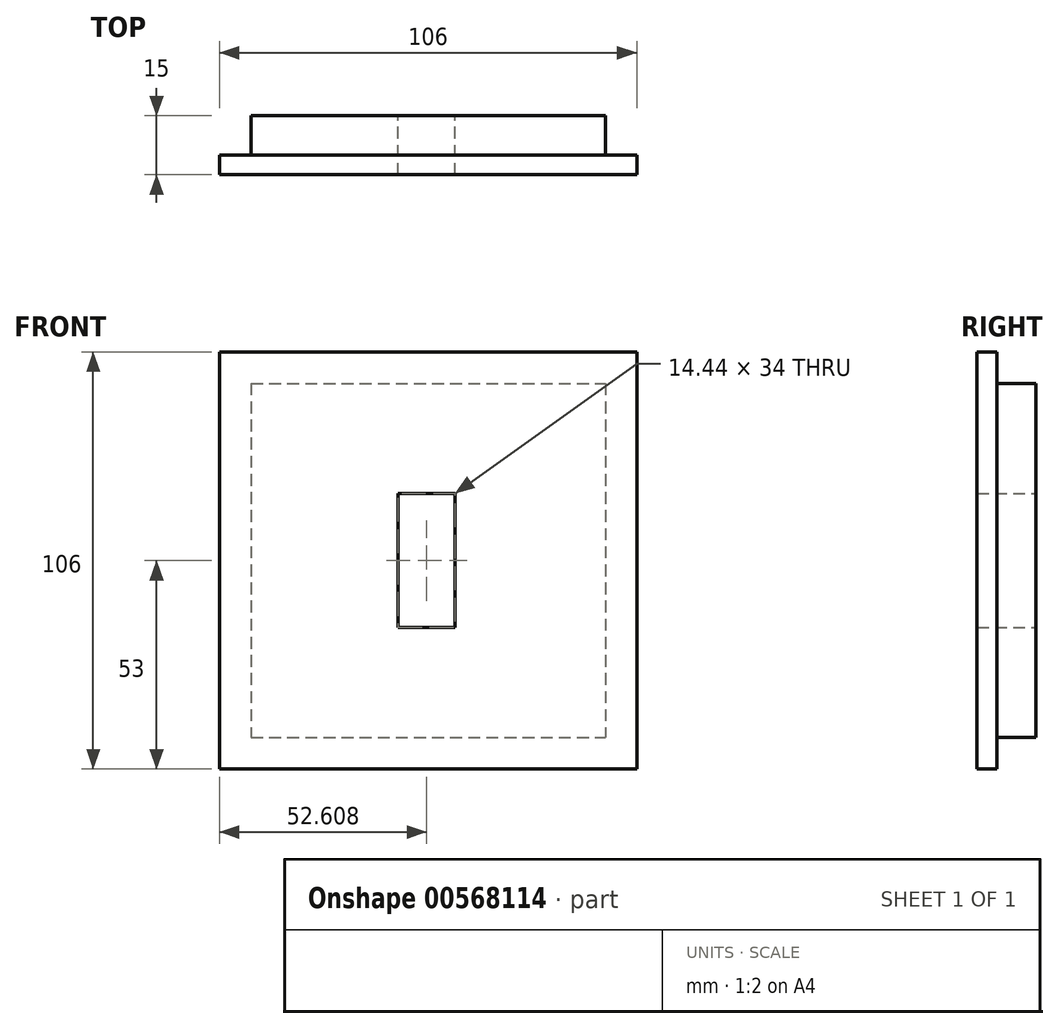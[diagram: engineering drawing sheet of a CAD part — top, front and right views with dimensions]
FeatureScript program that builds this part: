
annotation { "Feature Type Name" : "Feature", "Feature Type Description" : "" }
export const myFeature = defineFeature(function(context is Context, id is Id, definition is map)
    precondition{}
    {
        {
            var Q0;
            Q0=qCreatedBy(makeId("Front.planeOp"),FACE);
            var sketch = newSketch(context, id + "F0", { "sketchPlane" : qUnion([Q0])});
            skLineSegment(sketch, "E0.bottom", {"start": v(-43.54, 60.22) * mm, "end": v(46.46, 60.22) * mm});
            skLineSegment(sketch, "E0.top", {"start": v(-43.54, -29.78) * mm, "end": v(46.46, -29.78) * mm});
            skLineSegment(sketch, "E0.left", {"start": v(-43.54, 60.22) * mm, "end": v(-43.54, -29.78) * mm});
            skLineSegment(sketch, "E0.right", {"start": v(46.46, 60.22) * mm, "end": v(46.46, -29.78) * mm});
            skLineSegment(sketch, "E1.bottom", {"start": v(-51.54, 68.22) * mm, "end": v(54.46, 68.22) * mm});
            skLineSegment(sketch, "E1.top", {"start": v(-51.54, -37.78) * mm, "end": v(54.46, -37.78) * mm});
            skLineSegment(sketch, "E1.left", {"start": v(-51.54, 68.22) * mm, "end": v(-51.54, -37.78) * mm});
            skLineSegment(sketch, "E1.right", {"start": v(54.46, 68.22) * mm, "end": v(54.46, -37.78) * mm});
            skSolve(sketch);
        }
        {
            var Q0;
            Q0=makeQuery(id+"F0.imprint","IMPRINT",FACE,{"disambiguationData":[TD([[makeQuery(id+"F0.imprint","IMPRINT",EDGE,{"derivedFrom":sQuery(id+"F0.wireOp",EDGE,"E0.bottom")}),1.0]])]});
            var Q1;
            Q1=makeQuery(id+"F0.imprint","IMPRINT",FACE,{"disambiguationData":[TD([[makeQuery(id+"F0.imprint","IMPRINT",EDGE,{"derivedFrom":sQuery(id+"F0.wireOp",EDGE,"E0.bottom")}),-1.0]])]});
            extrude(context, id + "F1", {"entities" : qUnion([Q0, Q1]), "depth" : 15 * mm, "offsetDistance" : 25 * mm});
        }
        {
            var Q0;
            Q0=makeQuery(id+"F0.imprint","IMPRINT",FACE,{"disambiguationData":[TD([[makeQuery(id+"F0.imprint","IMPRINT",EDGE,{"derivedFrom":sQuery(id+"F0.wireOp",EDGE,"E0.bottom")}),1.0]])]});
            extrude(context, id + "F2", {"entities" : qUnion([Q0]), "operationType" : NewBodyOperationType.REMOVE, "depth" : 10 * mm, "offsetDistance" : 25 * mm});
        }
        {
            var Q0;
            Q0=makeQuery(id+"F1.opExtrude","CAP_FACE",FACE,{"disambiguationData":[OSD([sQuery(id+"F0.wireOp",EDGE,"E1.bottom"),sQuery(id+"F0.wireOp",EDGE,"E1.top"),sQuery(id+"F0.wireOp",EDGE,"E1.left"),sQuery(id+"F0.wireOp",EDGE,"E1.right")])],"isStart":true});
            var sketch = newSketch(context, id + "F3", { "sketchPlane" : qUnion([Q0])});
            skLineSegment(sketch, "E2.bottom", {"start": v(-8.29, 32.22) * mm, "end": v(6.15, 32.22) * mm});
            skLineSegment(sketch, "E2.top", {"start": v(-8.29, -1.78) * mm, "end": v(6.15, -1.78) * mm});
            skLineSegment(sketch, "E2.left", {"start": v(-8.29, 32.22) * mm, "end": v(-8.29, -1.78) * mm});
            skLineSegment(sketch, "E2.right", {"start": v(6.15, 32.22) * mm, "end": v(6.15, -1.78) * mm});
            skSolve(sketch);
        }
        {
            var Q0;
            Q0=makeQuery(id+"F3.imprint","IMPRINT",FACE,{"disambiguationData":[TD([[makeQuery(id+"F3.imprint","IMPRINT",EDGE,{"derivedFrom":sQuery(id+"F3.wireOp",EDGE,"E2.bottom")}),-1.0]])]});
            extrude(context, id + "F4", {"entities" : qUnion([Q0]), "operationType" : NewBodyOperationType.REMOVE, "oppositeDirection" : true, "depth" : 25 * mm, "offsetDistance" : 25 * mm});
        }
    });
